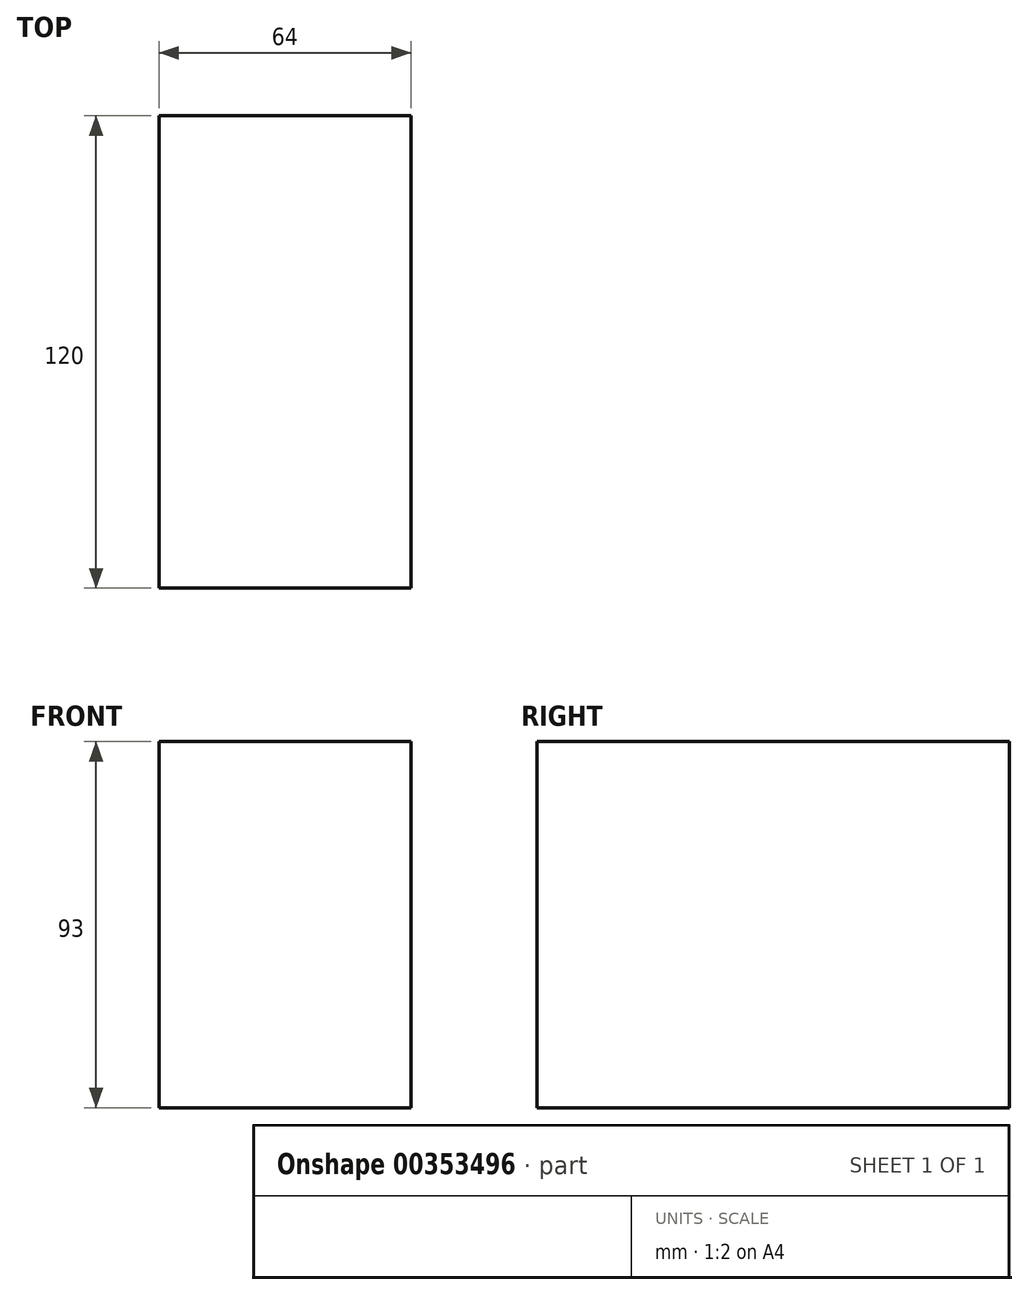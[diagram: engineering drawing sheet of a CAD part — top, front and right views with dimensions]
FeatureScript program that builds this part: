
annotation { "Feature Type Name" : "Feature", "Feature Type Description" : "" }
export const myFeature = defineFeature(function(context is Context, id is Id, definition is map)
    precondition{}
    {
        {
            var Q0;
            Q0=qCreatedBy(makeId("Front.planeOp"),FACE);
            var sketch = newSketch(context, id + "F0", { "sketchPlane" : qUnion([Q0])});
            skLineSegment(sketch, "E0.bottom", {"start": v(32, -46.5) * mm, "end": v(-32, -46.5) * mm});
            skLineSegment(sketch, "E0.top", {"start": v(32, 46.5) * mm, "end": v(-32, 46.5) * mm});
            skLineSegment(sketch, "E0.left", {"start": v(32, -46.5) * mm, "end": v(32, 46.5) * mm});
            skLineSegment(sketch, "E0.right", {"start": v(-32, -46.5) * mm, "end": v(-32, 46.5) * mm});
            skPoint(sketch, "E0.middle", {"position": v(0, 0) * mm});
            skSolve(sketch);
        }
        {
            var Q0;
            Q0=makeQuery(id+"F0.imprint","IMPRINT",FACE,{"disambiguationData":[TD([[makeQuery(id+"F0.imprint","IMPRINT",EDGE,{"derivedFrom":sQuery(id+"F0.wireOp",EDGE,"E0.bottom")}),-1.0]])]});
            extrude(context, id + "F1", {"entities" : qUnion([Q0]), "endBound" : BoundingType.SYMMETRIC, "depth" : 120 * mm});
        }
    });
